# Revit family: Faucet-Lavatory-KOHLER-COMPONENTS-K-77959T
name_source: partatom
category: Plumbing Fixtures
revit_build: Autodesk Revit 2017 (Build: 20160225_1515(x64)
units: mm (PartAtom-declared; Revit-internal decimal feet)

## family parameters
Cut with Voids When Loaded = No
Host = Face
OmniClass Number = 23.31.11.00
OmniClass Title = Faucets
Part Type = Normal
Room Calculation Point = No
Round Connector Dimension = Use Diameter
Shared = No

## types (11) — shared parameters
ADA Compliant = No
Assembly Code = D2010
CW Connection = Yes
Cold Water Inlet = Cold Water Inlet
Date Modified = 04/23/2020
Default Elevation = 36"
Description = Single handle bowl faucet
Flow Rate = 0 GPM
HW Connection = Yes
Handle Clearance = 3 5/8"
Height = 11 1/4"
Hot Water Inlet = Hot Water Inlet
Length = 7"
Manufacturer = KOHLER Co.
Master Format 2014 = 22 41 39
Master Format 2014 Name = Residential Faucets, Supplies, and Trim
Material = Premium Metal Construction
Pressure = 0.00 psi
Product Name = COMPONENTS
Spout Reach = 7"
URL = http://www.kohler.com.cn
Vent Connection = No
Waste Connection = No
Waste Water Outlet = Waste Water Outlet
WaterSense Certified = No
Width = 1 7/8"

## per-type parameters (varying)
| type | Drain Included | Finish | Lift Rod | Model | Product Documentation Link | Product Page URL | Type |
| With Drain, CP-Polished Chrome | Yes | Kohler-Metal-CP-Polished_Chrome | Yes | K-77959T-4A-CP | http://files.kohler.com.cn | http://www.kohler.com.cn | 1 |
| With Drain, BN-Roman silver | Yes | Kohler-Metal-BN-Roman_Silver | Yes | K-77959T-4A -BN | http://files.kohler.com.cn | http://www.kohler.com.cn | 2 |
| With Drain, 2BL-Original Black | Yes | Kohler-Metal-2BL-Original_Black | Yes | K-77959T-4A -2BL | http://files.kohler.com.cn | http://www.kohler.com.cn | 3 |
| With Drain, AF- Flange Gold | Yes | Kohler-Metal-AF-Flange_Gold | Yes | K-77959T-4A -AF | http://files.kohler.com.cn | http://www.kohler.com.cn | 4 |
| With Drain, RGD-Rose Gold | Yes | Kohler-Metal-RGD-Rose_Gold | Yes | K-77959T-4A -RGD | http://files.kohler.com.cn | http://www.kohler.com.cn | 5 |
| Without Drain, CP-Polished Chrome | No | Kohler-Metal-CP-Polished_Chrome | No | K-77959T-4AND-CP |  |  | 8 |
| With Drain, 3GC-Black Gold | Yes | Kohler-Metal-3GC-Black_Gold | Yes | K-77959T-4A-3GC | http://files.kohler.com.cn | http://www.kohler.com.cn | 6 |
| With Drain, TT- Titanium Silver | Yes | Kohler-Metal-TT-Titanium_Silver | Yes | K-77959T-4A-TT | http://files.kohler.com.cn | http://www.kohler.com.cn | 7 |
| Without Drain, AF- Flange Gold | No | Kohler-Metal-AF-Flange_Gold | No | K-77959T-4AND-AF |  |  | 9 |
| Without Drain, RGD-Rose Gold | No | Kohler-Metal-RGD-Rose_Gold | No | K-77959T-4AND-RGD |  |  | 10 |
| Without Drain, BN-Roman silver | No | Kohler-Metal-BN-Roman_Silver | No | K-77959T-4AND-BN |  |  | 11 |

## geometry (parser evidence)
native form markers: Sweep x6
no freeform markers — native parametric forms only
